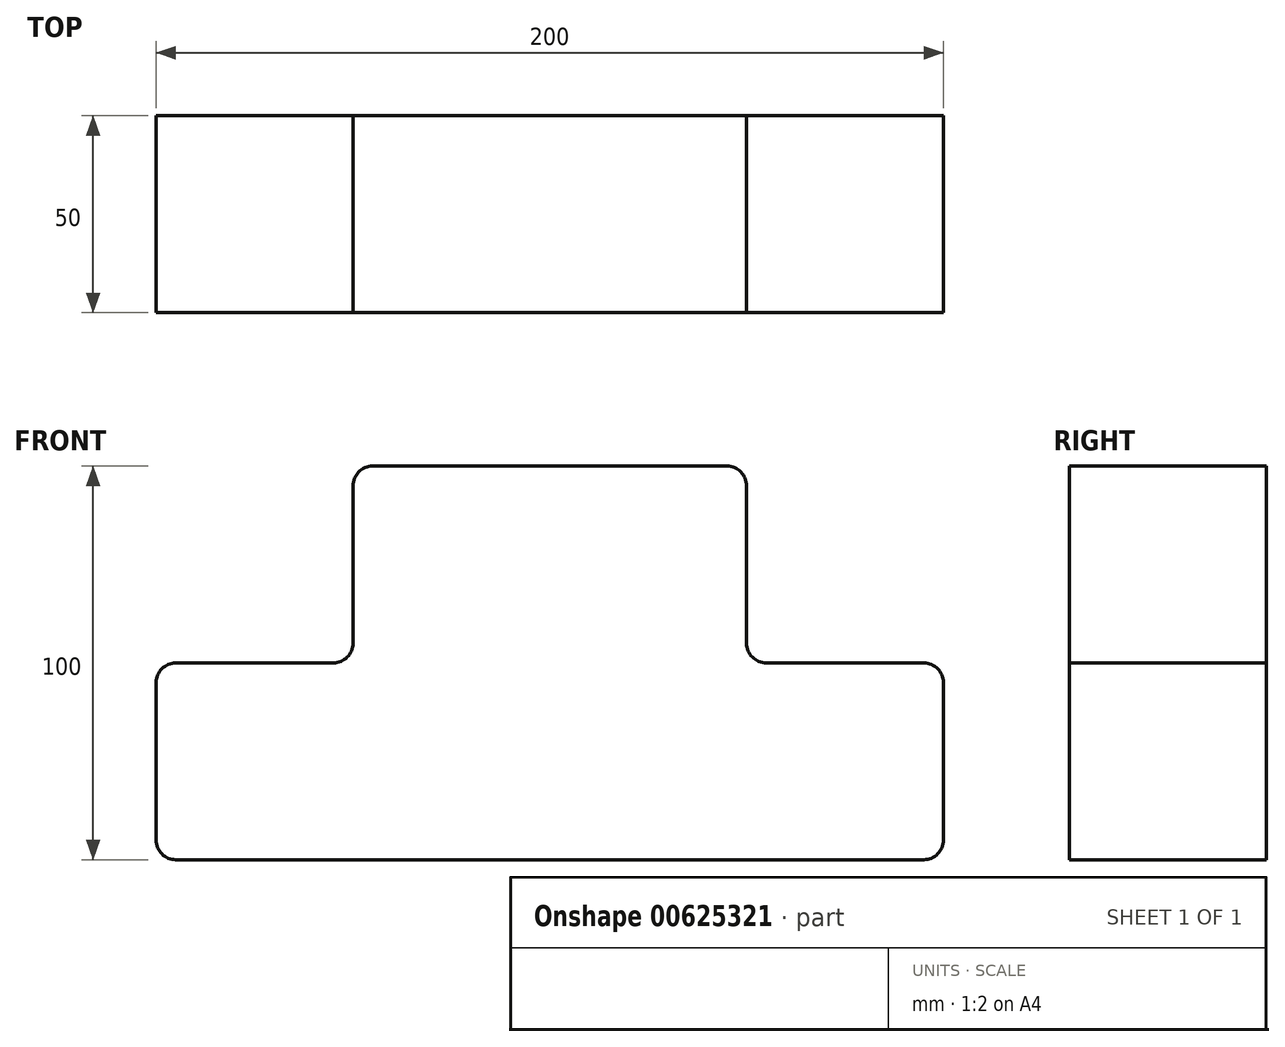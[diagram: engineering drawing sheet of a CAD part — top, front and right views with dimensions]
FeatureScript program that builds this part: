
annotation { "Feature Type Name" : "Feature", "Feature Type Description" : "" }
export const myFeature = defineFeature(function(context is Context, id is Id, definition is map)
    precondition{}
    {
        {
            var Q0;
            Q0=qCreatedBy(makeId("Front.planeOp"),FACE);
            var sketch = newSketch(context, id + "F0", { "sketchPlane" : qUnion([Q0])});
            skLineSegment(sketch, "E0.bottom", {"start": v(-5, 0) * mm, "end": v(-195, 0) * mm});
            skLineSegment(sketch, "E0.top", {"start": v(-5, 50) * mm, "end": v(-45, 50) * mm});
            skLineSegment(sketch, "E0.left", {"start": v(0, 5) * mm, "end": v(0, 45) * mm});
            skLineSegment(sketch, "E0.right", {"start": v(-200, 5) * mm, "end": v(-200, 45) * mm});
            skLineSegment(sketch, "E1.top", {"start": v(-145, 100) * mm, "end": v(-55, 100) * mm});
            skLineSegment(sketch, "E1.left", {"start": v(-150, 55) * mm, "end": v(-150, 95) * mm});
            skLineSegment(sketch, "E1.right", {"start": v(-50, 55) * mm, "end": v(-50, 95) * mm});
            skLineSegment(sketch, "E2.trimOffspring", {"start": v(-155, 50) * mm, "end": v(-195, 50) * mm});
            skPoint(sketch, "E3.visualSharp", {"position": v(-150, 50) * mm});
            skArc(sketch, "E3.filletArc", {"start": v(-155, 50) * mm, "mid": v(-151.46, 51.46) * mm, "end": v(-150, 55) * mm});
            skPoint(sketch, "E4.visualSharp", {"position": v(-50, 50) * mm});
            skArc(sketch, "E4.filletArc", {"start": v(-50, 55) * mm, "mid": v(-48.54, 51.46) * mm, "end": v(-45, 50) * mm});
            skPoint(sketch, "E5.visualSharp", {"position": v(-50, 100) * mm});
            skArc(sketch, "E5.filletArc", {"start": v(-50, 95) * mm, "mid": v(-51.46, 98.54) * mm, "end": v(-55, 100) * mm});
            skPoint(sketch, "E6.visualSharp", {"position": v(-150, 100) * mm});
            skArc(sketch, "E6.filletArc", {"start": v(-145, 100) * mm, "mid": v(-148.54, 98.54) * mm, "end": v(-150, 95) * mm});
            skPoint(sketch, "E7.visualSharp", {"position": v(-200, 50) * mm});
            skArc(sketch, "E7.filletArc", {"start": v(-195, 50) * mm, "mid": v(-198.54, 48.54) * mm, "end": v(-200, 45) * mm});
            skPoint(sketch, "E8.visualSharp", {"position": v(-200, 0) * mm});
            skArc(sketch, "E8.filletArc", {"start": v(-200, 5) * mm, "mid": v(-198.54, 1.46) * mm, "end": v(-195, 0) * mm});
            skPoint(sketch, "E9.visualSharp", {"position": v(0, 0) * mm});
            skArc(sketch, "E9.filletArc", {"start": v(-5, 0) * mm, "mid": v(-1.46, 1.46) * mm, "end": v(0, 5) * mm});
            skPoint(sketch, "E10.visualSharp", {"position": v(0, 50) * mm});
            skArc(sketch, "E10.filletArc", {"start": v(0, 45) * mm, "mid": v(-1.46, 48.54) * mm, "end": v(-5, 50) * mm});
            skSolve(sketch);
        }
        {
            var Q0;
            Q0 = qSketchRegion(id + "F0", true);
            extrude(context, id + "F1", {"entities" : qUnion([Q0]), "depth" : 50 * mm, "offsetDistance" : 25 * mm});
        }
    });
